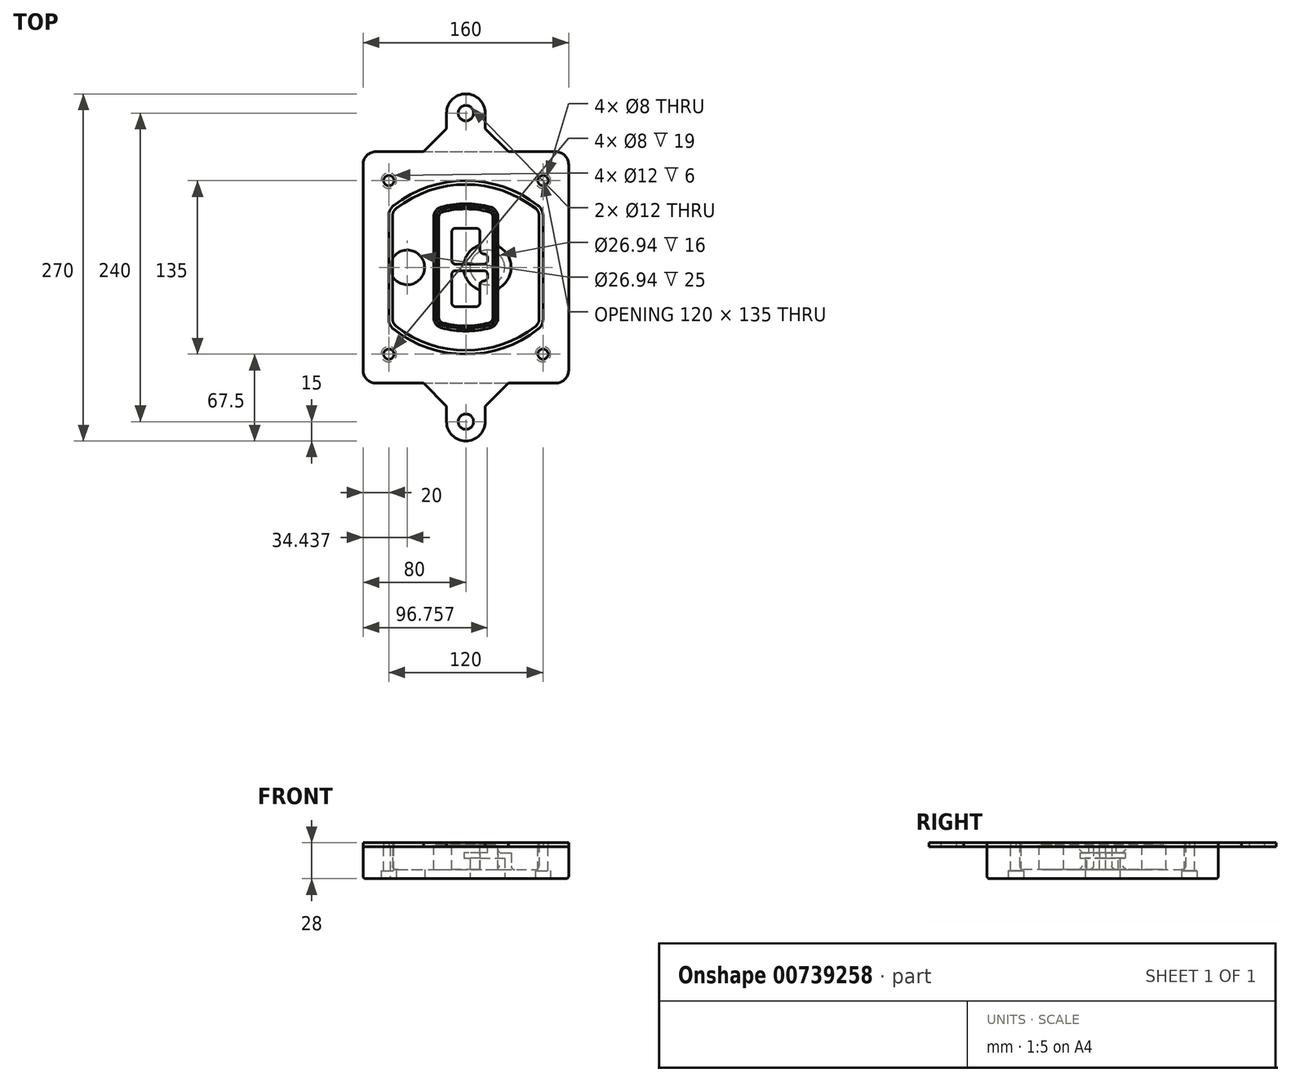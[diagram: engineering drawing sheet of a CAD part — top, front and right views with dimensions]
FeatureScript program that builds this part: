
annotation { "Feature Type Name" : "Feature", "Feature Type Description" : "" }
export const myFeature = defineFeature(function(context is Context, id is Id, definition is map)
    precondition{}
    {
        {
            var Q0;
            Q0=qCreatedBy(makeId("Top.planeOp"),FACE);
            var sketch = newSketch(context, id + "F0", { "sketchPlane" : qUnion([Q0])});
            skPoint(sketch, "E0.rect.middle", {"position": v(0, 0) * mm});
            skLineSegment(sketch, "E1.bottom", {"start": v(-70, -90) * mm, "end": v(70, -90) * mm});
            skLineSegment(sketch, "E1.top", {"start": v(-70, 90) * mm, "end": v(70, 90) * mm});
            skLineSegment(sketch, "E1.left", {"start": v(-80, -80) * mm, "end": v(-80, 80) * mm});
            skLineSegment(sketch, "E1.right", {"start": v(80, -80) * mm, "end": v(80, 80) * mm});
            skLineSegment(sketch, "E2", {"start": v(-80, 90) * mm, "end": v(80, -90) * mm, "construction": true});
            skLineSegment(sketch, "E3", {"start": v(80, 90) * mm, "end": v(-80, -90) * mm, "construction": true});
            skCircle(sketch, "E4", {"center": v(-60, 67.5) * mm, "radius": 4 * mm});
            skCircle(sketch, "E5", {"center": v(60, 67.5) * mm, "radius": 4 * mm});
            skCircle(sketch, "E6", {"center": v(60, -67.5) * mm, "radius": 4 * mm});
            skCircle(sketch, "E7", {"center": v(-60, -67.5) * mm, "radius": 4 * mm});
            skLineSegment(sketch, "E8", {"start": v(-60, 67.5) * mm, "end": v(60, 67.5) * mm, "construction": true});
            skLineSegment(sketch, "E9", {"start": v(60, 67.5) * mm, "end": v(60, -67.5) * mm, "construction": true});
            skLineSegment(sketch, "E10", {"start": v(60, -67.5) * mm, "end": v(-60, -67.5) * mm, "construction": true});
            skLineSegment(sketch, "E11", {"start": v(-60, -67.5) * mm, "end": v(-60, 67.5) * mm, "construction": true});
            skLineSegment(sketch, "E12", {"start": v(-60, 40.3) * mm, "end": v(-60, -40.3) * mm});
            skLineSegment(sketch, "E13", {"start": v(60, 40.3) * mm, "end": v(60, -40.3) * mm});
            skArc(sketch, "E14", {"start": v(56.15, 48.18) * mm, "mid": v(0, 67.5) * mm, "end": v(-56.15, 48.18) * mm});
            skArc(sketch, "E15", {"start": v(-56.15, -48.18) * mm, "mid": v(0, -67.5) * mm, "end": v(56.15, -48.18) * mm});
            skLineSegment(sketch, "E16", {"start": v(-60, 0) * mm, "end": v(60, 0) * mm, "construction": true});
            skPoint(sketch, "E17.visualSharp", {"position": v(-60, -45) * mm});
            skArc(sketch, "E17.filletArc", {"start": v(-60, -40.3) * mm, "mid": v(-58.99, -44.68) * mm, "end": v(-56.15, -48.18) * mm});
            skPoint(sketch, "E18.visualSharp", {"position": v(-60, 45) * mm});
            skArc(sketch, "E18.filletArc", {"start": v(-56.15, 48.18) * mm, "mid": v(-58.99, 44.68) * mm, "end": v(-60, 40.3) * mm});
            skPoint(sketch, "E19.visualSharp", {"position": v(60, 45) * mm});
            skArc(sketch, "E19.filletArc", {"start": v(60, 40.3) * mm, "mid": v(58.99, 44.68) * mm, "end": v(56.15, 48.18) * mm});
            skPoint(sketch, "E20.visualSharp", {"position": v(60, -45) * mm});
            skArc(sketch, "E20.filletArc", {"start": v(56.15, -48.18) * mm, "mid": v(58.99, -44.68) * mm, "end": v(60, -40.3) * mm});
            skPoint(sketch, "E21.visualSharp", {"position": v(-80, 90) * mm});
            skArc(sketch, "E21.filletArc", {"start": v(-70, 90) * mm, "mid": v(-77.07, 87.07) * mm, "end": v(-80, 80) * mm});
            skPoint(sketch, "E22.visualSharp", {"position": v(80, 90) * mm});
            skArc(sketch, "E22.filletArc", {"start": v(80, 80) * mm, "mid": v(77.07, 87.07) * mm, "end": v(70, 90) * mm});
            skPoint(sketch, "E23.visualSharp", {"position": v(80, -90) * mm});
            skArc(sketch, "E23.filletArc", {"start": v(70, -90) * mm, "mid": v(77.07, -87.07) * mm, "end": v(80, -80) * mm});
            skPoint(sketch, "E24.visualSharp", {"position": v(-80, -90) * mm});
            skArc(sketch, "E24.filletArc", {"start": v(-80, -80) * mm, "mid": v(-77.07, -87.07) * mm, "end": v(-70, -90) * mm});
            skArc(sketch, "E25.0", {"start": v(57, 40.3) * mm, "mid": v(56.3, 43.36) * mm, "end": v(54.3, 45.81) * mm});
            skLineSegment(sketch, "E25.1", {"start": v(57, 40.3) * mm, "end": v(57, -40.3) * mm});
            skArc(sketch, "E25.2", {"start": v(54.3, -45.81) * mm, "mid": v(56.3, -43.36) * mm, "end": v(57, -40.3) * mm});
            skArc(sketch, "E25.3", {"start": v(-54.3, -45.81) * mm, "mid": v(0, -64.5) * mm, "end": v(54.3, -45.81) * mm});
            skArc(sketch, "E25.4", {"start": v(-57, -40.3) * mm, "mid": v(-56.3, -43.36) * mm, "end": v(-54.3, -45.81) * mm});
            skArc(sketch, "E25.5", {"start": v(54.3, 45.81) * mm, "mid": v(0, 64.5) * mm, "end": v(-54.3, 45.81) * mm});
            skLineSegment(sketch, "E25.6", {"start": v(-57, 40.3) * mm, "end": v(-57, -40.3) * mm});
            skArc(sketch, "E25.7", {"start": v(-54.3, 45.81) * mm, "mid": v(-56.3, 43.36) * mm, "end": v(-57, 40.3) * mm});
            skArc(sketch, "E26.0", {"start": v(-58.62, 51.33) * mm, "mid": v(-62.58, 46.43) * mm, "end": v(-64, 40.3) * mm});
            skArc(sketch, "E26.1", {"start": v(58.62, 51.33) * mm, "mid": v(0, 71.5) * mm, "end": v(-58.62, 51.33) * mm});
            skArc(sketch, "E26.2", {"start": v(64, 40.3) * mm, "mid": v(62.58, 46.43) * mm, "end": v(58.62, 51.33) * mm});
            skLineSegment(sketch, "E26.3", {"start": v(64, 40.3) * mm, "end": v(64, -40.3) * mm});
            skArc(sketch, "E26.4", {"start": v(58.62, -51.33) * mm, "mid": v(62.58, -46.43) * mm, "end": v(64, -40.3) * mm});
            skLineSegment(sketch, "E26.5", {"start": v(-64, 40.3) * mm, "end": v(-64, -40.3) * mm});
            skArc(sketch, "E26.6", {"start": v(-58.62, -51.33) * mm, "mid": v(0, -71.5) * mm, "end": v(58.62, -51.33) * mm});
            skArc(sketch, "E26.7", {"start": v(-64, -40.3) * mm, "mid": v(-62.58, -46.43) * mm, "end": v(-58.62, -51.33) * mm});
            skSolve(sketch);
        }
        {
            var Q0;
            Q0=makeQuery(id+"F0.imprint","IMPRINT",FACE,{"disambiguationData":[TD([[makeQuery(id+"F0.imprint","IMPRINT",EDGE,{"derivedFrom":sQuery(id+"F0.wireOp",EDGE,"E1.bottom")}),1.0]])]});
            var Q1;
            Q1=makeQuery(id+"F0.imprint","IMPRINT",FACE,{"disambiguationData":[TD([[makeQuery(id+"F0.imprint","IMPRINT",EDGE,{"derivedFrom":sQuery(id+"F0.wireOp",EDGE,"E12")}),1.0]])]});
            var Q2;
            Q2=makeQuery(id+"F0.imprint","IMPRINT",FACE,{"disambiguationData":[TD([[makeQuery(id+"F0.imprint","IMPRINT",EDGE,{"derivedFrom":sQuery(id+"F0.wireOp",EDGE,"E25.0")}),1.0]])]});
            var Q3;
            Q3=makeQuery(id+"F0.imprint","IMPRINT",FACE,{"disambiguationData":[TD([[makeQuery(id+"F0.imprint","IMPRINT",EDGE,{"derivedFrom":sQuery(id+"F0.wireOp",EDGE,"E12")}),-1.0]])]});
            extrude(context, id + "F1", {"entities" : qUnion([Q0, Q1, Q2, Q3]), "oppositeDirection" : true, "depth" : 25 * mm});
        }
        {
            var Q0;
            Q0=makeQuery(id+"F0.imprint","IMPRINT",FACE,{"disambiguationData":[TD([[makeQuery(id+"F0.imprint","IMPRINT",EDGE,{"derivedFrom":sQuery(id+"F0.wireOp",EDGE,"E12")}),1.0]])]});
            extrude(context, id + "F2", {"entities" : qUnion([Q0]), "operationType" : NewBodyOperationType.ADD, "depth" : 3 * mm});
        }
        {
            var Q0;
            Q0=makeQuery(id+"F0.imprint","IMPRINT",FACE,{"disambiguationData":[TD([[makeQuery(id+"F0.imprint","IMPRINT",EDGE,{"derivedFrom":sQuery(id+"F0.wireOp",EDGE,"E25.0")}),1.0]])]});
            extrude(context, id + "F3", {"entities" : qUnion([Q0]), "operationType" : NewBodyOperationType.REMOVE, "oppositeDirection" : true, "depth" : 18 * mm});
        }
        {
            var Q0;
            Q0=makeQuery(id+"F2.opExtrude","CAP_FACE",FACE,{"disambiguationData":[OSD([sQuery(id+"F0.wireOp",EDGE,"E12"),sQuery(id+"F0.wireOp",EDGE,"E13"),sQuery(id+"F0.wireOp",EDGE,"E14"),sQuery(id+"F0.wireOp",EDGE,"E15"),sQuery(id+"F0.wireOp",EDGE,"E17.filletArc"),sQuery(id+"F0.wireOp",EDGE,"E18.filletArc"),sQuery(id+"F0.wireOp",EDGE,"E19.filletArc"),sQuery(id+"F0.wireOp",EDGE,"E20.filletArc"),sQuery(id+"F0.wireOp",EDGE,"E25.0"),sQuery(id+"F0.wireOp",EDGE,"E25.1"),sQuery(id+"F0.wireOp",EDGE,"E25.2"),sQuery(id+"F0.wireOp",EDGE,"E25.3"),sQuery(id+"F0.wireOp",EDGE,"E25.4"),sQuery(id+"F0.wireOp",EDGE,"E25.5"),sQuery(id+"F0.wireOp",EDGE,"E25.6"),sQuery(id+"F0.wireOp",EDGE,"E25.7")])],"isStart":false});
            var sketch = newSketch(context, id + "F4", { "sketchPlane" : qUnion([Q0])});
            skArc(sketch, "E27.0", {"start": v(-19.08, -46.97) * mm, "mid": v(0, -49.5) * mm, "end": v(19.08, -46.97) * mm});
            skArc(sketch, "E28.0", {"start": v(19.08, 46.97) * mm, "mid": v(0, 49.5) * mm, "end": v(-19.08, 46.97) * mm});
            skLineSegment(sketch, "E29", {"start": v(-25, 39.25) * mm, "end": v(-25, -39.25) * mm});
            skLineSegment(sketch, "E30", {"start": v(25, 39.25) * mm, "end": v(25, -39.25) * mm});
            skLineSegment(sketch, "E31", {"start": v(-25, 45.1) * mm, "end": v(25, 45.1) * mm, "construction": true});
            skLineSegment(sketch, "E32", {"start": v(-25, -45.1) * mm, "end": v(25, -45.1) * mm, "construction": true});
            skPoint(sketch, "E33.visualSharp", {"position": v(-25, 45.1) * mm});
            skArc(sketch, "E33.filletArc", {"start": v(-19.08, 46.97) * mm, "mid": v(-23.35, 44.11) * mm, "end": v(-25, 39.25) * mm});
            skPoint(sketch, "E34.visualSharp", {"position": v(25, 45.1) * mm});
            skArc(sketch, "E34.filletArc", {"start": v(25, 39.25) * mm, "mid": v(23.35, 44.11) * mm, "end": v(19.08, 46.97) * mm});
            skPoint(sketch, "E35.visualSharp", {"position": v(25, -45.1) * mm});
            skArc(sketch, "E35.filletArc", {"start": v(19.08, -46.97) * mm, "mid": v(23.35, -44.11) * mm, "end": v(25, -39.25) * mm});
            skPoint(sketch, "E36.visualSharp", {"position": v(-25, -45.1) * mm});
            skArc(sketch, "E36.filletArc", {"start": v(-25, -39.25) * mm, "mid": v(-23.35, -44.11) * mm, "end": v(-19.08, -46.97) * mm});
            skArc(sketch, "E37.0", {"start": v(54.3, 45.81) * mm, "mid": v(0, 64.5) * mm, "end": v(-54.3, 45.81) * mm});
            skArc(sketch, "E37.1", {"start": v(-54.3, 45.81) * mm, "mid": v(-56.3, 43.36) * mm, "end": v(-57, 40.3) * mm});
            skLineSegment(sketch, "E37.2", {"start": v(-57, 40.3) * mm, "end": v(-57, -40.3) * mm});
            skArc(sketch, "E37.3", {"start": v(-57, -40.3) * mm, "mid": v(-56.3, -43.36) * mm, "end": v(-54.3, -45.81) * mm});
            skArc(sketch, "E37.4", {"start": v(-54.3, -45.81) * mm, "mid": v(0, -64.5) * mm, "end": v(54.3, -45.81) * mm});
            skArc(sketch, "E37.5", {"start": v(54.3, -45.81) * mm, "mid": v(56.3, -43.36) * mm, "end": v(57, -40.3) * mm});
            skLineSegment(sketch, "E37.6", {"start": v(57, 40.3) * mm, "end": v(57, -40.3) * mm});
            skArc(sketch, "E37.7", {"start": v(57, 40.3) * mm, "mid": v(56.3, 43.36) * mm, "end": v(54.3, 45.81) * mm});
            skLineSegment(sketch, "E38.0", {"start": v(23, 39.25) * mm, "end": v(23, -39.25) * mm});
            skArc(sketch, "E38.1", {"start": v(18.56, -45.04) * mm, "mid": v(21.76, -42.9) * mm, "end": v(23, -39.25) * mm});
            skArc(sketch, "E38.2", {"start": v(-18.56, -45.04) * mm, "mid": v(0, -47.5) * mm, "end": v(18.56, -45.04) * mm});
            skArc(sketch, "E38.3", {"start": v(-23, -39.25) * mm, "mid": v(-21.76, -42.9) * mm, "end": v(-18.56, -45.04) * mm});
            skLineSegment(sketch, "E38.4", {"start": v(-23, 39.25) * mm, "end": v(-23, -39.25) * mm});
            skArc(sketch, "E38.5", {"start": v(23, 39.25) * mm, "mid": v(21.76, 42.9) * mm, "end": v(18.56, 45.04) * mm});
            skArc(sketch, "E38.6", {"start": v(-18.56, 45.04) * mm, "mid": v(-21.76, 42.9) * mm, "end": v(-23, 39.25) * mm});
            skArc(sketch, "E38.7", {"start": v(18.56, 45.04) * mm, "mid": v(0, 47.5) * mm, "end": v(-18.56, 45.04) * mm});
            skArc(sketch, "E39.0", {"start": v(21, 39.25) * mm, "mid": v(20.18, 41.68) * mm, "end": v(18.04, 43.1) * mm});
            skLineSegment(sketch, "E39.1", {"start": v(21, 39.25) * mm, "end": v(21, -39.25) * mm});
            skArc(sketch, "E39.2", {"start": v(18.04, -43.1) * mm, "mid": v(20.18, -41.68) * mm, "end": v(21, -39.25) * mm});
            skArc(sketch, "E39.3", {"start": v(-18.04, -43.1) * mm, "mid": v(0, -45.5) * mm, "end": v(18.04, -43.1) * mm});
            skArc(sketch, "E39.4", {"start": v(-21, -39.25) * mm, "mid": v(-20.18, -41.68) * mm, "end": v(-18.04, -43.1) * mm});
            skArc(sketch, "E39.5", {"start": v(18.04, 43.1) * mm, "mid": v(0, 45.5) * mm, "end": v(-18.04, 43.1) * mm});
            skLineSegment(sketch, "E39.6", {"start": v(-21, 39.25) * mm, "end": v(-21, -39.25) * mm});
            skArc(sketch, "E39.7", {"start": v(-18.04, 43.1) * mm, "mid": v(-20.18, 41.68) * mm, "end": v(-21, 39.25) * mm});
            skLineSegment(sketch, "E40", {"start": v(-25, 0) * mm, "end": v(25, 0) * mm, "construction": true});
            skLineSegment(sketch, "E41", {"start": v(-11, 5.5) * mm, "end": v(-11, 27.5) * mm});
            skLineSegment(sketch, "E42", {"start": v(-8, 30.5) * mm, "end": v(8, 30.5) * mm});
            skLineSegment(sketch, "E43", {"start": v(11, 27.5) * mm, "end": v(11, 13.5) * mm});
            skLineSegment(sketch, "E44", {"start": v(14, 10.5) * mm, "end": v(14, 10.5) * mm});
            skLineSegment(sketch, "E45", {"start": v(17, 7.5) * mm, "end": v(17, 5.5) * mm});
            skLineSegment(sketch, "E46", {"start": v(14, 2.5) * mm, "end": v(-8, 2.5) * mm});
            skPoint(sketch, "E47.visualSharp", {"position": v(-11, 30.5) * mm});
            skArc(sketch, "E47.filletArc", {"start": v(-8, 30.5) * mm, "mid": v(-10.12, 29.62) * mm, "end": v(-11, 27.5) * mm});
            skPoint(sketch, "E48.visualSharp", {"position": v(11, 30.5) * mm});
            skArc(sketch, "E48.filletArc", {"start": v(11, 27.5) * mm, "mid": v(10.12, 29.62) * mm, "end": v(8, 30.5) * mm});
            skPoint(sketch, "E49.visualSharp", {"position": v(11, 10.5) * mm});
            skArc(sketch, "E49.filletArc", {"start": v(11, 13.5) * mm, "mid": v(11.88, 11.38) * mm, "end": v(14, 10.5) * mm});
            skPoint(sketch, "E50.visualSharp", {"position": v(17, 10.5) * mm});
            skArc(sketch, "E50.filletArc", {"start": v(17, 7.5) * mm, "mid": v(16.12, 9.62) * mm, "end": v(14, 10.5) * mm});
            skPoint(sketch, "E51.visualSharp", {"position": v(17, 2.5) * mm});
            skArc(sketch, "E51.filletArc", {"start": v(14, 2.5) * mm, "mid": v(16.12, 3.38) * mm, "end": v(17, 5.5) * mm});
            skPoint(sketch, "E52.visualSharp", {"position": v(-11, 2.5) * mm});
            skArc(sketch, "E52.filletArc", {"start": v(-11, 5.5) * mm, "mid": v(-10.12, 3.38) * mm, "end": v(-8, 2.5) * mm});
            skLineSegment(sketch, "E53.0.MirrorCS", {"start": v(14, -2.5) * mm, "end": v(-8, -2.5) * mm});
            skArc(sketch, "E54.0.MirrorCS", {"start": v(-11, -5.5) * mm, "mid": v(-10.12, -3.38) * mm, "end": v(-8, -2.5) * mm});
            skLineSegment(sketch, "E55.0.MirrorCS", {"start": v(-11, -5.5) * mm, "end": v(-11, -27.5) * mm});
            skArc(sketch, "E56.0.MirrorCS", {"start": v(-8, -30.5) * mm, "mid": v(-10.12, -29.62) * mm, "end": v(-11, -27.5) * mm});
            skLineSegment(sketch, "E57.0.MirrorCS", {"start": v(-8, -30.5) * mm, "end": v(8, -30.5) * mm});
            skArc(sketch, "E58.0.MirrorCS", {"start": v(11, -27.5) * mm, "mid": v(10.12, -29.62) * mm, "end": v(8, -30.5) * mm});
            skLineSegment(sketch, "E59.0.MirrorCS", {"start": v(11, -27.5) * mm, "end": v(11, -13.5) * mm});
            skArc(sketch, "E60.0.MirrorCS", {"start": v(11, -13.5) * mm, "mid": v(11.88, -11.38) * mm, "end": v(14, -10.5) * mm});
            skArc(sketch, "E61.0.MirrorCS", {"start": v(17, -7.5) * mm, "mid": v(16.12, -9.62) * mm, "end": v(14, -10.5) * mm});
            skLineSegment(sketch, "E62.0.MirrorCS", {"start": v(17, -7.5) * mm, "end": v(17, -5.5) * mm});
            skArc(sketch, "E63.0.MirrorCS", {"start": v(14, -2.5) * mm, "mid": v(16.12, -3.38) * mm, "end": v(17, -5.5) * mm});
            skSolve(sketch);
        }
        {
            var Q0;
            Q0=makeQuery(id+"F4.imprint","IMPRINT",FACE,{"disambiguationData":[TD([[makeQuery(id+"F4.imprint","IMPRINT",EDGE,{"derivedFrom":sQuery(id+"F4.wireOp",EDGE,"E27.0")}),1.0]])]});
            var Q1;
            Q1=makeQuery(id+"F4.imprint","IMPRINT",FACE,{"disambiguationData":[TD([[makeQuery(id+"F4.imprint","IMPRINT",EDGE,{"derivedFrom":sQuery(id+"F4.wireOp",EDGE,"E38.0")}),-1.0]])]});
            var Q2;
            Q2=makeQuery(id+"F4.imprint","IMPRINT",FACE,{"disambiguationData":[TD([[makeQuery(id+"F4.imprint","IMPRINT",EDGE,{"derivedFrom":sQuery(id+"F4.wireOp",EDGE,"E39.0")}),1.0]])]});
            extrude(context, id + "F5", {"entities" : qUnion([Q0, Q1, Q2]), "operationType" : NewBodyOperationType.ADD, "endBound" : BoundingType.UP_TO_NEXT, "oppositeDirection" : true, "depth" : 25 * mm});
        }
        {
            var Q0;
            Q0=makeQuery(id+"F4.imprint","IMPRINT",FACE,{"disambiguationData":[TD([[makeQuery(id+"F4.imprint","IMPRINT",EDGE,{"derivedFrom":sQuery(id+"F4.wireOp",EDGE,"E38.0")}),-1.0]])]});
            extrude(context, id + "F6", {"entities" : qUnion([Q0]), "operationType" : NewBodyOperationType.REMOVE, "oppositeDirection" : true, "depth" : 2 * mm});
        }
        {
            var Q0;
            Q0=makeQuery(id+"F1.opExtrude","CAP_FACE",FACE,{"disambiguationData":[OSD([sQuery(id+"F0.wireOp",EDGE,"E1.bottom"),sQuery(id+"F0.wireOp",EDGE,"E1.top"),sQuery(id+"F0.wireOp",EDGE,"E1.left"),sQuery(id+"F0.wireOp",EDGE,"E1.right"),sQuery(id+"F0.wireOp",EDGE,"E4"),sQuery(id+"F0.wireOp",EDGE,"E5"),sQuery(id+"F0.wireOp",EDGE,"E6"),sQuery(id+"F0.wireOp",EDGE,"E7"),sQuery(id+"F0.wireOp",EDGE,"E21.filletArc"),sQuery(id+"F0.wireOp",EDGE,"E22.filletArc"),sQuery(id+"F0.wireOp",EDGE,"E23.filletArc"),sQuery(id+"F0.wireOp",EDGE,"E24.filletArc")])],"isStart":false});
            var sketch = newSketch(context, id + "F7", { "sketchPlane" : qUnion([Q0])});
            skCircle(sketch, "E64", {"center": v(16.76, 0) * mm, "radius": 13.47 * mm});
            skCircle(sketch, "E65", {"center": v(-45.56, 0) * mm, "radius": 13.47 * mm});
            skLineSegment(sketch, "E66", {"start": v(80, 0) * mm, "end": v(-80, 0) * mm});
            skCircle(sketch, "E67", {"center": v(16.76, 0) * mm, "radius": 18.47 * mm});
            skCircle(sketch, "E68", {"center": v(60, -67.5) * mm, "radius": 6 * mm});
            skCircle(sketch, "E69", {"center": v(-60, -67.5) * mm, "radius": 6 * mm});
            skCircle(sketch, "E70", {"center": v(-60, 67.5) * mm, "radius": 6 * mm});
            skCircle(sketch, "E71", {"center": v(60, 67.5) * mm, "radius": 6 * mm});
            skSolve(sketch);
        }
        {
            var Q0;
            {var subQ1=sQuery(id+"F7.wireOp",EDGE,"E66");var subQ4=sQuery(id+"F7.wireOp",EDGE,"E64");var subQ6=makeQuery(id+"F7.imprint","INTERSECT",VERTEX,{"disambiguationData":[OD(0.0)],"derivedFrom":[subQ4,subQ1]});Q0=makeQuery(id+"F7.imprint","IMPRINT",FACE,{"disambiguationData":[TD([[makeQuery(id+"F7.imprint","IMPRINT",EDGE,{"disambiguationData":[TD([[subQ6,-1.0]])],"derivedFrom":subQ4}),-1.0]])]});}
            var Q1;
            {var subQ0=sQuery(id+"F7.wireOp",EDGE,"E66");var subQ1=sQuery(id+"F7.wireOp",EDGE,"E64");var subQ3=makeQuery(id+"F7.imprint","INTERSECT",VERTEX,{"disambiguationData":[OD(0.0)],"derivedFrom":[subQ1,subQ0]});Q1=makeQuery(id+"F7.imprint","IMPRINT",FACE,{"disambiguationData":[TD([[makeQuery(id+"F7.imprint","IMPRINT",EDGE,{"disambiguationData":[TD([[subQ3,-1.0]])],"derivedFrom":subQ1}),1.0]])]});}
            var Q2;
            {var subQ0=sQuery(id+"F7.wireOp",EDGE,"E66");var subQ1=sQuery(id+"F7.wireOp",EDGE,"E64");var subQ3=makeQuery(id+"F7.imprint","INTERSECT",VERTEX,{"disambiguationData":[OD(0.0)],"derivedFrom":[subQ1,subQ0]});Q2=makeQuery(id+"F7.imprint","IMPRINT",FACE,{"disambiguationData":[TD([[makeQuery(id+"F7.imprint","IMPRINT",EDGE,{"disambiguationData":[TD([[subQ3,1.0]])],"derivedFrom":subQ1}),1.0]])]});}
            var Q3;
            {var subQ1=sQuery(id+"F7.wireOp",EDGE,"E66");var subQ4=sQuery(id+"F7.wireOp",EDGE,"E64");var subQ6=makeQuery(id+"F7.imprint","INTERSECT",VERTEX,{"disambiguationData":[OD(0.0)],"derivedFrom":[subQ4,subQ1]});Q3=makeQuery(id+"F7.imprint","IMPRINT",FACE,{"disambiguationData":[TD([[makeQuery(id+"F7.imprint","IMPRINT",EDGE,{"disambiguationData":[TD([[subQ6,1.0]])],"derivedFrom":subQ4}),-1.0]])]});}
            extrude(context, id + "F8", {"entities" : qUnion([Q0, Q1, Q2, Q3]), "operationType" : NewBodyOperationType.ADD, "oppositeDirection" : true, "depth" : 20 * mm});
        }
        {
            var Q0;
            {var subQ0=sQuery(id+"F7.wireOp",EDGE,"E66");var subQ1=sQuery(id+"F7.wireOp",EDGE,"E64");var subQ3=makeQuery(id+"F7.imprint","INTERSECT",VERTEX,{"disambiguationData":[OD(0.0)],"derivedFrom":[subQ1,subQ0]});Q0=makeQuery(id+"F7.imprint","IMPRINT",FACE,{"disambiguationData":[TD([[makeQuery(id+"F7.imprint","IMPRINT",EDGE,{"disambiguationData":[TD([[subQ3,-1.0]])],"derivedFrom":subQ1}),1.0]])]});}
            var Q1;
            {var subQ0=sQuery(id+"F7.wireOp",EDGE,"E66");var subQ1=sQuery(id+"F7.wireOp",EDGE,"E64");var subQ3=makeQuery(id+"F7.imprint","INTERSECT",VERTEX,{"disambiguationData":[OD(0.0)],"derivedFrom":[subQ1,subQ0]});Q1=makeQuery(id+"F7.imprint","IMPRINT",FACE,{"disambiguationData":[TD([[makeQuery(id+"F7.imprint","IMPRINT",EDGE,{"disambiguationData":[TD([[subQ3,1.0]])],"derivedFrom":subQ1}),1.0]])]});}
            extrude(context, id + "F9", {"entities" : qUnion([Q0, Q1]), "operationType" : NewBodyOperationType.REMOVE, "oppositeDirection" : true, "depth" : 16 * mm});
        }
        {
            var Q0;
            {var subQ0=sQuery(id+"F7.wireOp",EDGE,"E66");var subQ1=sQuery(id+"F7.wireOp",EDGE,"E65");var subQ3=makeQuery(id+"F7.imprint","INTERSECT",VERTEX,{"disambiguationData":[OD(0.0)],"derivedFrom":[subQ1,subQ0]});Q0=makeQuery(id+"F7.imprint","IMPRINT",FACE,{"disambiguationData":[TD([[makeQuery(id+"F7.imprint","IMPRINT",EDGE,{"disambiguationData":[TD([[subQ3,-1.0]])],"derivedFrom":subQ1}),1.0]])]});}
            var Q1;
            {var subQ0=sQuery(id+"F7.wireOp",EDGE,"E66");var subQ1=sQuery(id+"F7.wireOp",EDGE,"E65");var subQ3=makeQuery(id+"F7.imprint","INTERSECT",VERTEX,{"disambiguationData":[OD(0.0)],"derivedFrom":[subQ1,subQ0]});Q1=makeQuery(id+"F7.imprint","IMPRINT",FACE,{"disambiguationData":[TD([[makeQuery(id+"F7.imprint","IMPRINT",EDGE,{"disambiguationData":[TD([[subQ3,1.0]])],"derivedFrom":subQ1}),1.0]])]});}
            extrude(context, id + "F10", {"entities" : qUnion([Q0, Q1]), "operationType" : NewBodyOperationType.REMOVE, "oppositeDirection" : true, "depth" : 25 * mm});
        }
        {
            var Q0;
            Q0=makeQuery(id+"F7.imprint","IMPRINT",FACE,{"disambiguationData":[TD([[makeQuery(id+"F7.imprint","IMPRINT",EDGE,{"derivedFrom":sQuery(id+"F7.wireOp",EDGE,"E68")}),1.0]])]});
            var Q1;
            Q1=makeQuery(id+"F7.imprint","IMPRINT",FACE,{"disambiguationData":[TD([[makeQuery(id+"F7.imprint","IMPRINT",EDGE,{"derivedFrom":makeQuery(id+"F1.opExtrude","CAP_EDGE",EDGE,{"disambiguationData":[OSD([sQuery(id+"F0.wireOp",EDGE,"E5")])],"isStart":false})}),-1.0]])]});
            var Q2;
            Q2=makeQuery(id+"F7.imprint","IMPRINT",FACE,{"disambiguationData":[TD([[makeQuery(id+"F7.imprint","IMPRINT",EDGE,{"derivedFrom":sQuery(id+"F7.wireOp",EDGE,"E69")}),1.0]])]});
            var Q3;
            Q3=makeQuery(id+"F7.imprint","IMPRINT",FACE,{"disambiguationData":[TD([[makeQuery(id+"F7.imprint","IMPRINT",EDGE,{"derivedFrom":makeQuery(id+"F1.opExtrude","CAP_EDGE",EDGE,{"disambiguationData":[OSD([sQuery(id+"F0.wireOp",EDGE,"E4")])],"isStart":false})}),-1.0]])]});
            var Q4;
            Q4=makeQuery(id+"F7.imprint","IMPRINT",FACE,{"disambiguationData":[TD([[makeQuery(id+"F7.imprint","IMPRINT",EDGE,{"derivedFrom":sQuery(id+"F7.wireOp",EDGE,"E70")}),1.0]])]});
            var Q5;
            Q5=makeQuery(id+"F7.imprint","IMPRINT",FACE,{"disambiguationData":[TD([[makeQuery(id+"F7.imprint","IMPRINT",EDGE,{"derivedFrom":makeQuery(id+"F1.opExtrude","CAP_EDGE",EDGE,{"disambiguationData":[OSD([sQuery(id+"F0.wireOp",EDGE,"E7")])],"isStart":false})}),-1.0]])]});
            var Q6;
            Q6=makeQuery(id+"F7.imprint","IMPRINT",FACE,{"disambiguationData":[TD([[makeQuery(id+"F7.imprint","IMPRINT",EDGE,{"derivedFrom":sQuery(id+"F7.wireOp",EDGE,"E71")}),1.0]])]});
            var Q7;
            Q7=makeQuery(id+"F7.imprint","IMPRINT",FACE,{"disambiguationData":[TD([[makeQuery(id+"F7.imprint","IMPRINT",EDGE,{"derivedFrom":makeQuery(id+"F1.opExtrude","CAP_EDGE",EDGE,{"disambiguationData":[OSD([sQuery(id+"F0.wireOp",EDGE,"E6")])],"isStart":false})}),-1.0]])]});
            extrude(context, id + "F11", {"entities" : qUnion([Q0, Q1, Q2, Q3, Q4, Q5, Q6, Q7]), "operationType" : NewBodyOperationType.REMOVE, "oppositeDirection" : true, "depth" : 6 * mm});
        }
        {
            var Q0;
            Q0=makeQuery(id+"F9.boolean.opBoolean","COPY",FACE,{"derivedFrom":makeQuery(id+"F9.opExtrude","CAP_FACE",FACE,{"disambiguationData":[OSD([sQuery(id+"F7.wireOp",EDGE,"E64")])],"isStart":false})});
            var sketch = newSketch(context, id + "F12", { "sketchPlane" : qUnion([Q0])});
            skArc(sketch, "E72.0", {"start": v(11, 17.55) * mm, "mid": v(2.57, 11.82) * mm, "end": v(-1.54, 2.5) * mm});
            skArc(sketch, "E72.1", {"start": v(-1.54, -2.5) * mm, "mid": v(2.57, -11.82) * mm, "end": v(11, -17.55) * mm});
            skLineSegment(sketch, "E73", {"start": v(-1.54, -2.5) * mm, "end": v(14, -2.5) * mm});
            skLineSegment(sketch, "E74.0", {"start": v(14, 2.5) * mm, "end": v(-1.54, 2.5) * mm});
            skArc(sketch, "E74.1", {"start": v(14, 2.5) * mm, "mid": v(16.12, 3.38) * mm, "end": v(17, 5.5) * mm});
            skLineSegment(sketch, "E74.2", {"start": v(17, 7.5) * mm, "end": v(17, 5.5) * mm});
            skArc(sketch, "E74.3", {"start": v(17, 7.5) * mm, "mid": v(16.12, 9.62) * mm, "end": v(14, 10.5) * mm});
            skArc(sketch, "E74.4", {"start": v(11, 13.5) * mm, "mid": v(11.88, 11.38) * mm, "end": v(14, 10.5) * mm});
            skLineSegment(sketch, "E74.5", {"start": v(11, 17.55) * mm, "end": v(11, 13.5) * mm});
            skLineSegment(sketch, "E74.7", {"start": v(14, -2.5) * mm, "end": v(-1.54, -2.5) * mm});
            skArc(sketch, "E74.8", {"start": v(14, -2.5) * mm, "mid": v(16.12, -3.38) * mm, "end": v(17, -5.5) * mm});
            skLineSegment(sketch, "E74.9", {"start": v(17, -7.5) * mm, "end": v(17, -5.5) * mm});
            skArc(sketch, "E74.10", {"start": v(17, -7.5) * mm, "mid": v(16.12, -9.62) * mm, "end": v(14, -10.5) * mm});
            skArc(sketch, "E74.11", {"start": v(11, -13.5) * mm, "mid": v(11.88, -11.38) * mm, "end": v(14, -10.5) * mm});
            skLineSegment(sketch, "E74.12", {"start": v(11, -17.55) * mm, "end": v(11, -13.5) * mm});
            skPoint(sketch, "E75.orphan", {"position": v(11, -27.5) * mm});
            skPoint(sketch, "E76.orphan", {"position": v(-8, -2.5) * mm});
            skPoint(sketch, "E77.orphan", {"position": v(-8, 2.5) * mm});
            skPoint(sketch, "E78.orphan", {"position": v(11, 27.5) * mm});
            skSolve(sketch);
        }
        {
            var Q0;
            {var subQ7=sQuery(id+"F12.wireOp",EDGE,"E72.0");var subQ14=sQuery(id+"F12.wireOp",EDGE,"E72.1");var subQ16=sQuery(id+"F12.wireOp",EDGE,"E74.1");var subQ18=sQuery(id+"F12.wireOp",EDGE,"E74.8");Q0=qUnion([makeQuery(id+"F12.imprint","IMPRINT",FACE,{"disambiguationData":[TD([[makeQuery(id+"F12.imprint","IMPRINT",EDGE,{"derivedFrom":subQ7}),1.0]])]}),makeQuery(id+"F12.imprint","IMPRINT",FACE,{"disambiguationData":[TD([[makeQuery(id+"F12.imprint","IMPRINT",EDGE,{"derivedFrom":subQ14}),1.0]])]}),makeQuery(id+"F12.imprint","IMPRINT",FACE,{"disambiguationData":[TD([[makeQuery(id+"F12.imprint","IMPRINT",EDGE,{"derivedFrom":subQ16}),1.0]])]}),makeQuery(id+"F12.imprint","IMPRINT",FACE,{"disambiguationData":[TD([[makeQuery(id+"F12.imprint","IMPRINT",EDGE,{"derivedFrom":subQ18}),-1.0]])]})]);}
            var Q1;
            Q1=makeQuery(id+"F5.boolean.opBoolean","SPLIT",FACE,{"disambiguationData":[TD([makeQuery(id+"F5.opExtrude","SWEPT_FACE",FACE,{"disambiguationData":[OSD([sQuery(id+"F4.wireOp",EDGE,"E41")])]})])],"derivedFrom":makeQuery(id+"F3.boolean.opBoolean","COPY",FACE,{"derivedFrom":makeQuery(id+"F3.opExtrude","CAP_FACE",FACE,{"disambiguationData":[OSD([sQuery(id+"F0.wireOp",EDGE,"E25.0"),sQuery(id+"F0.wireOp",EDGE,"E25.1"),sQuery(id+"F0.wireOp",EDGE,"E25.2"),sQuery(id+"F0.wireOp",EDGE,"E25.3"),sQuery(id+"F0.wireOp",EDGE,"E25.4"),sQuery(id+"F0.wireOp",EDGE,"E25.5"),sQuery(id+"F0.wireOp",EDGE,"E25.6"),sQuery(id+"F0.wireOp",EDGE,"E25.7")])],"isStart":false})})});
            extrude(context, id + "F13", {"entities" : qUnion([Q0]), "operationType" : NewBodyOperationType.REMOVE, "endBound" : BoundingType.UP_TO_SURFACE, "endBoundEntityFace" : qUnion([Q1]), "depth" : 25 * mm});
        }
        {
            var Q0;
            Q0=makeQuery(id+"F3.boolean.opBoolean","COPY",EDGE,{"derivedFrom":makeQuery(id+"F3.opExtrude","CAP_EDGE",EDGE,{"disambiguationData":[OSD([sQuery(id+"F0.wireOp",EDGE,"E25.6")])],"isStart":false})});
            var Q1;
            Q1=makeQuery(id+"F8.boolean.opBoolean","INTERSECT",EDGE,{"derivedFrom":[makeQuery(id+"F5.opExtrude","SWEPT_FACE",FACE,{"disambiguationData":[OSD([sQuery(id+"F4.wireOp",EDGE,"E30")])]}),makeQuery(id+"F8.opExtrude","CAP_FACE",FACE,{"disambiguationData":[OSD([sQuery(id+"F7.wireOp",EDGE,"E67")])],"isStart":false})]});
            var Q2;
            Q2=makeQuery(id+"F8.boolean.opBoolean","INTERSECT",EDGE,{"disambiguationData":[OD(1.0)],"derivedFrom":[makeQuery(id+"F5.opExtrude","SWEPT_FACE",FACE,{"disambiguationData":[OSD([sQuery(id+"F4.wireOp",EDGE,"E30")])]}),makeQuery(id+"F8.opExtrude","SWEPT_FACE",FACE,{"disambiguationData":[OSD([sQuery(id+"F7.wireOp",EDGE,"E67")])]})]});
            var Q3;
            {var subQ0=makeQuery(id+"F3.boolean.opBoolean","COPY",FACE,{"derivedFrom":makeQuery(id+"F3.opExtrude","CAP_FACE",FACE,{"disambiguationData":[OSD([sQuery(id+"F0.wireOp",EDGE,"E25.0"),sQuery(id+"F0.wireOp",EDGE,"E25.1"),sQuery(id+"F0.wireOp",EDGE,"E25.2"),sQuery(id+"F0.wireOp",EDGE,"E25.3"),sQuery(id+"F0.wireOp",EDGE,"E25.4"),sQuery(id+"F0.wireOp",EDGE,"E25.5"),sQuery(id+"F0.wireOp",EDGE,"E25.6"),sQuery(id+"F0.wireOp",EDGE,"E25.7")])],"isStart":false})});var subQ1=sQuery(id+"F4.wireOp",EDGE,"E30");Q3=makeQuery(id+"F8.boolean.opBoolean","SPLIT",EDGE,{"disambiguationData":[TD([makeQuery(id+"F5.opExtrude","SWEPT_FACE",FACE,{"disambiguationData":[OSD([sQuery(id+"F4.wireOp",EDGE,"E35.filletArc")])]})])],"derivedFrom":makeQuery(id+"F5.opExtrude","TWEAK_EDGE",EDGE,{"derivedFrom":[subQ0,makeQuery(id+"F4.imprint","IMPRINT",EDGE,{"derivedFrom":subQ1})]})});}
            var Q4;
            {var subQ0=sQuery(id+"F0.wireOp",EDGE,"E25.0");var subQ1=sQuery(id+"F0.wireOp",EDGE,"E25.1");var subQ2=sQuery(id+"F0.wireOp",EDGE,"E25.2");var subQ3=sQuery(id+"F0.wireOp",EDGE,"E25.3");var subQ4=sQuery(id+"F0.wireOp",EDGE,"E25.4");var subQ5=sQuery(id+"F0.wireOp",EDGE,"E25.5");var subQ6=sQuery(id+"F0.wireOp",EDGE,"E25.6");var subQ7=sQuery(id+"F0.wireOp",EDGE,"E25.7");Q4=makeQuery(id+"F8.boolean.opBoolean","INTERSECT",EDGE,{"derivedFrom":[makeQuery(id+"F5.boolean.opBoolean","SPLIT",FACE,{"disambiguationData":[TD([makeQuery(id+"F2.opExtrude","SWEPT_FACE",FACE,{"disambiguationData":[OSD([subQ0])]})])],"derivedFrom":makeQuery(id+"F3.boolean.opBoolean","COPY",FACE,{"derivedFrom":makeQuery(id+"F3.opExtrude","CAP_FACE",FACE,{"disambiguationData":[OSD([subQ0,subQ1,subQ2,subQ3,subQ4,subQ5,subQ6,subQ7])],"isStart":false})})}),makeQuery(id+"F8.opExtrude","SWEPT_FACE",FACE,{"disambiguationData":[OSD([sQuery(id+"F7.wireOp",EDGE,"E67")])]})]});}
            var Q5;
            Q5=makeQuery(id+"F8.boolean.opBoolean","INTERSECT",EDGE,{"disambiguationData":[OD(0.0)],"derivedFrom":[makeQuery(id+"F5.opExtrude","SWEPT_FACE",FACE,{"disambiguationData":[OSD([sQuery(id+"F4.wireOp",EDGE,"E30")])]}),makeQuery(id+"F8.opExtrude","SWEPT_FACE",FACE,{"disambiguationData":[OSD([sQuery(id+"F7.wireOp",EDGE,"E67")])]})]});
            fillet(context, id + "F14", {"entities" : qUnion([Q0, Q1, Q2, Q3, Q4, Q5]), "radius" : 3 * mm, "tangentPropagation" : true, "allowEdgeOverflow" : false});
        }
        {
            var Q0;
            Q0=makeQuery(id+"F1.opExtrude","CAP_EDGE",EDGE,{"disambiguationData":[OSD([sQuery(id+"F0.wireOp",EDGE,"E1.bottom")])],"isStart":false});
            fillet(context, id + "F15", {"entities" : qUnion([Q0]), "radius" : 2 * mm, "tangentPropagation" : true, "allowEdgeOverflow" : false});
        }
        {
            var Q0;
            {var subQ0=sQuery(id+"F0.wireOp",EDGE,"E21.filletArc");var subQ1=sQuery(id+"F0.wireOp",EDGE,"E7");var subQ2=sQuery(id+"F0.wireOp",EDGE,"E6");var subQ3=sQuery(id+"F0.wireOp",EDGE,"E5");var subQ4=sQuery(id+"F0.wireOp",EDGE,"E4");var subQ5=sQuery(id+"F0.wireOp",EDGE,"E22.filletArc");var subQ6=sQuery(id+"F0.wireOp",EDGE,"E1.bottom");var subQ7=sQuery(id+"F0.wireOp",EDGE,"E1.right");var subQ8=sQuery(id+"F0.wireOp",EDGE,"E1.top");var subQ9=sQuery(id+"F0.wireOp",EDGE,"E1.left");var subQ10=sQuery(id+"F0.wireOp",EDGE,"E23.filletArc");var subQ11=sQuery(id+"F0.wireOp",EDGE,"E24.filletArc");Q0=makeQuery(id+"F2.boolean.opBoolean","SPLIT",FACE,{"disambiguationData":[TD([makeQuery(id+"F1.opExtrude","SWEPT_FACE",FACE,{"disambiguationData":[OSD([subQ6])]})])],"derivedFrom":makeQuery(id+"F1.opExtrude","CAP_FACE",FACE,{"disambiguationData":[OSD([subQ6,subQ8,subQ9,subQ7,subQ4,subQ3,subQ2,subQ1,subQ0,subQ5,subQ10,subQ11])],"isStart":true})});}
            var sketch = newSketch(context, id + "F16", { "sketchPlane" : qUnion([Q0])});
            skLineSegment(sketch, "E79", {"start": v(0, 90) * mm, "end": v(0, 120) * mm, "construction": true});
            skCircle(sketch, "E80", {"center": v(0, 120) * mm, "radius": 6 * mm});
            skArc(sketch, "E81", {"start": v(15, 120) * mm, "mid": v(0, 135) * mm, "end": v(-15, 120) * mm});
            skLineSegment(sketch, "E82", {"start": v(-15, 120) * mm, "end": v(-15, 108) * mm});
            skLineSegment(sketch, "E83", {"start": v(15, 120) * mm, "end": v(15, 108) * mm});
            skLineSegment(sketch, "E84", {"start": v(-15, 108) * mm, "end": v(-33, 90) * mm});
            skLineSegment(sketch, "E85", {"start": v(15, 108) * mm, "end": v(33, 90) * mm});
            skLineSegment(sketch, "E86", {"start": v(-80, 0) * mm, "end": v(80, 0) * mm, "construction": true});
            skLineSegment(sketch, "E87", {"start": v(0, -90) * mm, "end": v(0, -120) * mm, "construction": true});
            skCircle(sketch, "E88", {"center": v(0, -120) * mm, "radius": 6 * mm});
            skArc(sketch, "E89", {"start": v(-15, -120) * mm, "mid": v(0, -135) * mm, "end": v(15, -120) * mm});
            skLineSegment(sketch, "E90", {"start": v(-15, -120) * mm, "end": v(-15, -108) * mm});
            skLineSegment(sketch, "E91", {"start": v(15, -120) * mm, "end": v(15, -108) * mm});
            skLineSegment(sketch, "E92", {"start": v(-15, -108) * mm, "end": v(-33, -90) * mm});
            skLineSegment(sketch, "E93", {"start": v(15, -108) * mm, "end": v(33, -90) * mm});
            skSolve(sketch);
        }
        {
            var Q0;
            Q0=makeQuery(id+"F16.imprint","IMPRINT",FACE,{"disambiguationData":[TD([[makeQuery(id+"F16.imprint","IMPRINT",EDGE,{"derivedFrom":sQuery(id+"F16.wireOp",EDGE,"E80")}),-1.0]])]});
            var Q1;
            Q1=makeQuery(id+"F16.imprint","IMPRINT",FACE,{"disambiguationData":[TD([[makeQuery(id+"F16.imprint","IMPRINT",EDGE,{"derivedFrom":makeQuery(id+"F1.opExtrude","CAP_EDGE",EDGE,{"disambiguationData":[OSD([sQuery(id+"F0.wireOp",EDGE,"E1.left")])],"isStart":true})}),-1.0]])]});
            var Q2;
            Q2=makeQuery(id+"F16.imprint","IMPRINT",FACE,{"disambiguationData":[TD([[makeQuery(id+"F16.imprint","IMPRINT",EDGE,{"derivedFrom":sQuery(id+"F16.wireOp",EDGE,"E88")}),-1.0]])]});
            var Q3;
            Q3=makeQuery(id+"F2.opExtrude","CAP_FACE",FACE,{"disambiguationData":[OSD([sQuery(id+"F0.wireOp",EDGE,"E12"),sQuery(id+"F0.wireOp",EDGE,"E13"),sQuery(id+"F0.wireOp",EDGE,"E14"),sQuery(id+"F0.wireOp",EDGE,"E15"),sQuery(id+"F0.wireOp",EDGE,"E17.filletArc"),sQuery(id+"F0.wireOp",EDGE,"E18.filletArc"),sQuery(id+"F0.wireOp",EDGE,"E19.filletArc"),sQuery(id+"F0.wireOp",EDGE,"E20.filletArc"),sQuery(id+"F0.wireOp",EDGE,"E25.0"),sQuery(id+"F0.wireOp",EDGE,"E25.1"),sQuery(id+"F0.wireOp",EDGE,"E25.2"),sQuery(id+"F0.wireOp",EDGE,"E25.3"),sQuery(id+"F0.wireOp",EDGE,"E25.4"),sQuery(id+"F0.wireOp",EDGE,"E25.5"),sQuery(id+"F0.wireOp",EDGE,"E25.6"),sQuery(id+"F0.wireOp",EDGE,"E25.7")])],"isStart":false});
            extrude(context, id + "F17", {"entities" : qUnion([Q0, Q1, Q2]), "endBound" : BoundingType.UP_TO_SURFACE, "depth" : 25 * mm, "endBoundEntityFace" : qUnion([Q3]), "offsetDistance" : 25 * mm});
        }
    });
